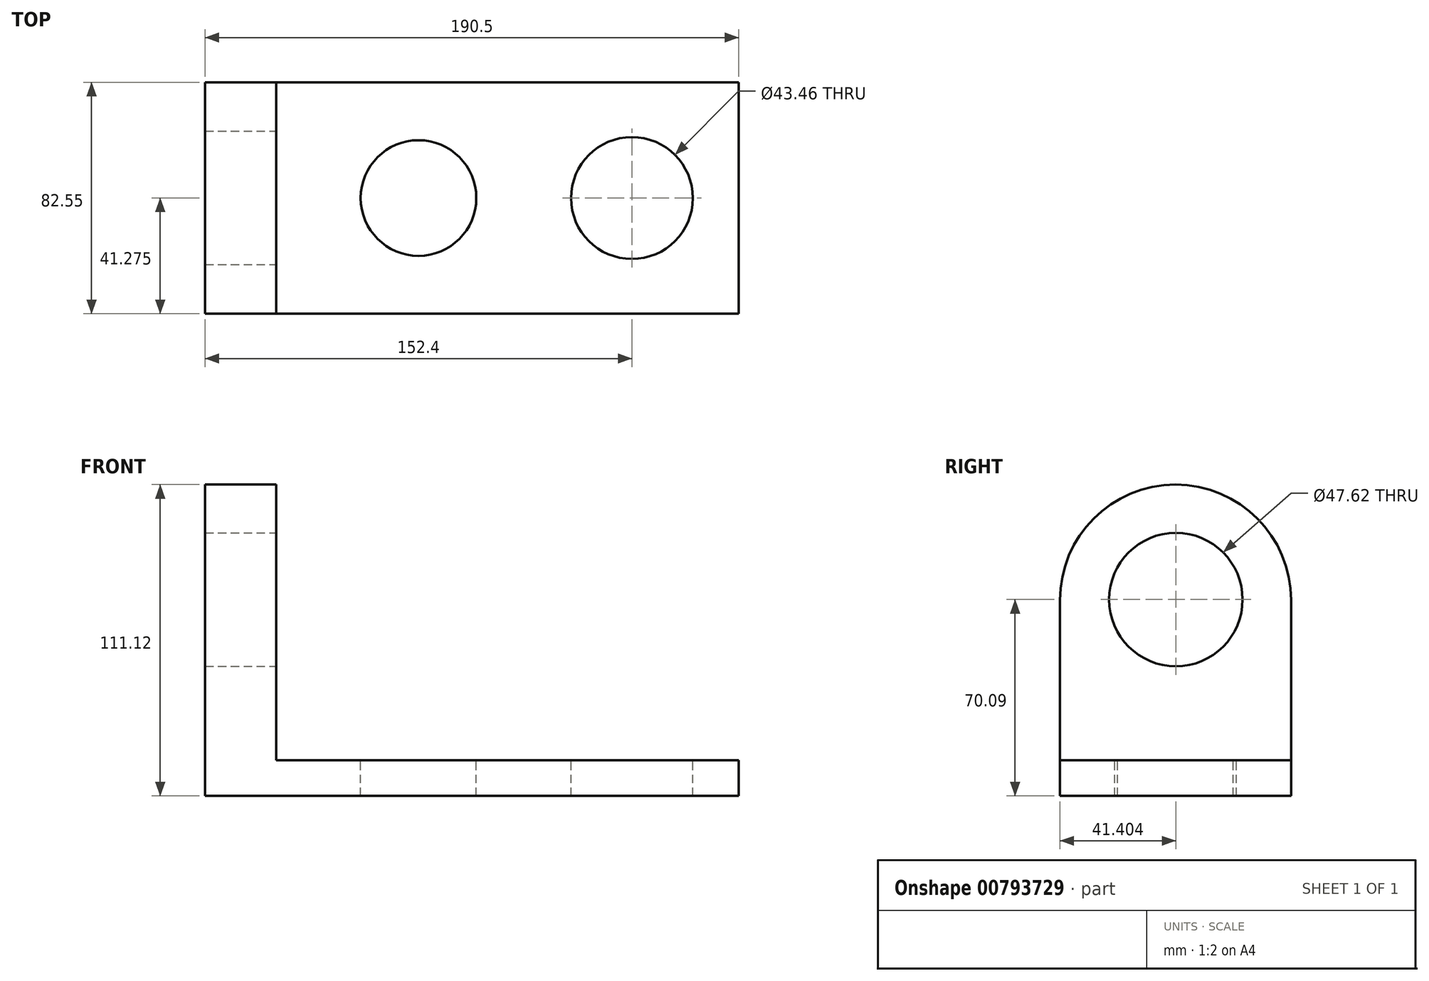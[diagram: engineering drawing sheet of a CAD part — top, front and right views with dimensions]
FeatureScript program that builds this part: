
annotation { "Feature Type Name" : "Feature", "Feature Type Description" : "" }
export const myFeature = defineFeature(function(context is Context, id is Id, definition is map)
    precondition{}
    {
        {
            var Q0;
            Q0=qCreatedBy(makeId("Front.planeOp"),FACE);
            var sketch = newSketch(context, id + "F0", { "sketchPlane" : qUnion([Q0])});
            skLineSegment(sketch, "E0", {"start": v(0, 0) * mm, "end": v(190.5, 0) * mm});
            skLineSegment(sketch, "E1", {"start": v(0, 0) * mm, "end": v(0, 57.15) * mm});
            skLineSegment(sketch, "E2", {"start": v(0, 57.15) * mm, "end": v(25.4, 57.15) * mm});
            skLineSegment(sketch, "E3", {"start": v(25.4, 57.15) * mm, "end": v(25.4, 12.7) * mm});
            skLineSegment(sketch, "E4", {"start": v(190.5, 0) * mm, "end": v(190.5, 12.7) * mm});
            skLineSegment(sketch, "E5", {"start": v(190.5, 12.7) * mm, "end": v(25.4, 12.7) * mm});
            skSolve(sketch);
        }
        {
            var Q0;
            Q0 = qSketchRegion(id + "F0", true);
            extrude(context, id + "F1", {"entities" : qUnion([Q0]), "depth" : 82.55 * mm, "offsetDistance" : 25.4 * mm});
        }
        {
            var Q0;
            Q0=makeQuery(id+"F1.opExtrude","CAP_FACE",FACE,{"disambiguationData":[OSD([sQuery(id+"F0.wireOp",EDGE,"E0"),sQuery(id+"F0.wireOp",EDGE,"E1"),sQuery(id+"F0.wireOp",EDGE,"E2"),sQuery(id+"F0.wireOp",EDGE,"E3"),sQuery(id+"F0.wireOp",EDGE,"E4"),sQuery(id+"F0.wireOp",EDGE,"E5")])],"isStart":false});
            var sketch = newSketch(context, id + "F2", { "sketchPlane" : qUnion([Q0])});
            skLineSegment(sketch, "E6", {"start": v(0, 57.15) * mm, "end": v(0, 127) * mm});
            skLineSegment(sketch, "E7", {"start": v(0, 127) * mm, "end": v(25.4, 127) * mm});
            skLineSegment(sketch, "E8", {"start": v(25.4, 127) * mm, "end": v(25.4, 57.15) * mm});
            skSolve(sketch);
        }
        {
            var Q0;
            Q0=makeQuery(id+"F2.imprint","IMPRINT",FACE,{"disambiguationData":[TD([[makeQuery(id+"F2.imprint","IMPRINT",EDGE,{"derivedFrom":sQuery(id+"F2.wireOp",EDGE,"E6")}),-1.0]])]});
            extrude(context, id + "F3", {"entities" : qUnion([Q0]), "operationType" : NewBodyOperationType.ADD, "oppositeDirection" : true, "depth" : 82.55 * mm, "offsetDistance" : 25.4 * mm});
        }
        {
            var Q0;
            Q0=makeQuery(id+"F1.opExtrude","SWEPT_FACE",FACE,{"disambiguationData":[OSD([sQuery(id+"F0.wireOp",EDGE,"E5")])]});
            var sketch = newSketch(context, id + "F4", { "sketchPlane" : qUnion([Q0])});
            skLineSegment(sketch, "E9", {"start": v(25.4, -41.28) * mm, "end": v(76.2, -41.28) * mm, "construction": true});
            skLineSegment(sketch, "E10", {"start": v(76.2, -41.28) * mm, "end": v(152.4, -41.28) * mm, "construction": true});
            skLineSegment(sketch, "E11", {"start": v(152.4, -41.28) * mm, "end": v(190.5, -41.28) * mm, "construction": true});
            skCircle(sketch, "E12", {"center": v(152.4, -41.28) * mm, "radius": 21.73 * mm});
            skCircle(sketch, "E13", {"center": v(76.2, -41.28) * mm, "radius": 20.64 * mm});
            skSolve(sketch);
        }
        {
            var Q0;
            Q0=makeQuery(id+"F4.imprint","IMPRINT",FACE,{"disambiguationData":[TD([[makeQuery(id+"F4.imprint","IMPRINT",EDGE,{"derivedFrom":sQuery(id+"F4.wireOp",EDGE,"E13")}),1.0]])]});
            var Q1;
            Q1=makeQuery(id+"F4.imprint","IMPRINT",FACE,{"disambiguationData":[TD([[makeQuery(id+"F4.imprint","IMPRINT",EDGE,{"derivedFrom":sQuery(id+"F4.wireOp",EDGE,"E12")}),1.0]])]});
            extrude(context, id + "F5", {"entities" : qUnion([Q0, Q1]), "operationType" : NewBodyOperationType.REMOVE, "oppositeDirection" : true, "depth" : 25.4 * mm, "offsetDistance" : 25.4 * mm});
        }
        {
            var Q0;
            Q0=makeQuery(id+"F3.boolean.opBoolean","MERGE",FACE,{"derivedFrom":[makeQuery(id+"F1.opExtrude","SWEPT_FACE",FACE,{"disambiguationData":[OSD([sQuery(id+"F0.wireOp",EDGE,"E3")])]}),makeQuery(id+"F3.opExtrude","SWEPT_FACE",FACE,{"disambiguationData":[OSD([sQuery(id+"F2.wireOp",EDGE,"E8")])]})]});
            var sketch = newSketch(context, id + "F6", { "sketchPlane" : qUnion([Q0])});
            skLineSegment(sketch, "E14", {"start": v(-82.55, 12.7) * mm, "end": v(-82.55, 69.85) * mm, "construction": true});
            skLineSegment(sketch, "E15", {"start": v(-82.55, 69.85) * mm, "end": v(0, 69.85) * mm, "construction": true});
            skLineSegment(sketch, "E16", {"start": v(-41.28, 127) * mm, "end": v(-41.28, 12.7) * mm, "construction": true});
            skArc(sketch, "E17", {"start": v(0, 69.85) * mm, "mid": v(-41.27, 111.13) * mm, "end": v(-82.55, 69.85) * mm});
            skSolve(sketch);
        }
        {
            var Q0;
            {var subQ0=sQuery(id+"F6.wireOp",EDGE,"E17");Q0=makeQuery(id+"F6.imprint","IMPRINT",FACE,{"disambiguationData":[TD([[makeQuery(id+"F6.imprint","IMPRINT",EDGE,{"derivedFrom":subQ0}),-1.0]])]});}
            extrude(context, id + "F7", {"entities" : qUnion([Q0]), "operationType" : NewBodyOperationType.REMOVE, "oppositeDirection" : true, "depth" : 25.4 * mm, "offsetDistance" : 25.4 * mm});
        }
        {
            var Q0;
            {var subQ0=sQuery(id+"F6.wireOp",EDGE,"E17");Q0=makeQuery(id+"F6.imprint","IMPRINT",FACE,{"disambiguationData":[TD([[makeQuery(id+"F6.imprint","IMPRINT",EDGE,{"derivedFrom":subQ0}),1.0]])]});}
            var sketch = newSketch(context, id + "F8", { "sketchPlane" : qUnion([Q0])});
            skCircle(sketch, "E18", {"center": v(-41.15, 70.09) * mm, "radius": 23.81 * mm});
            skSolve(sketch);
        }
        {
            var Q0;
            Q0=makeQuery(id+"F8.imprint","IMPRINT",FACE,{"disambiguationData":[TD([[makeQuery(id+"F8.imprint","IMPRINT",EDGE,{"derivedFrom":sQuery(id+"F8.wireOp",EDGE,"E18")}),1.0]])]});
            extrude(context, id + "F9", {"entities" : qUnion([Q0]), "operationType" : NewBodyOperationType.REMOVE, "oppositeDirection" : true, "depth" : 25.4 * mm, "offsetDistance" : 25.4 * mm});
        }
    });
